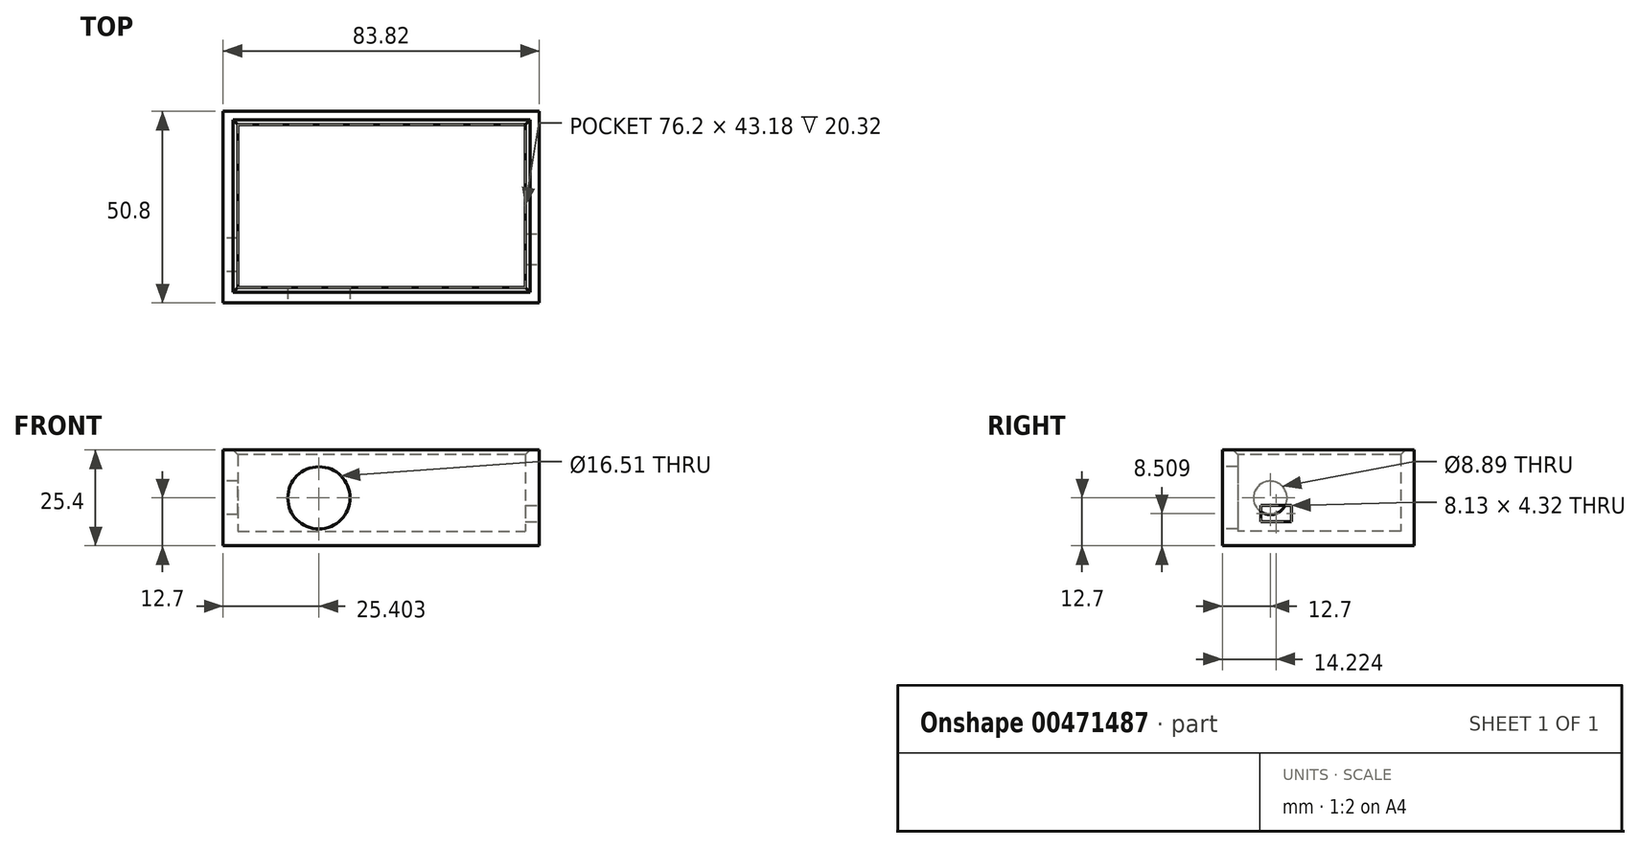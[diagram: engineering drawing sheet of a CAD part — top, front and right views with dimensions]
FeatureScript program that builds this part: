
annotation { "Feature Type Name" : "Feature", "Feature Type Description" : "" }
export const myFeature = defineFeature(function(context is Context, id is Id, definition is map)
    precondition{}
    {
        {
            var Q0;
            Q0=qCreatedBy(makeId("Top.planeOp"),FACE);
            var sketch = newSketch(context, id + "F0", { "sketchPlane" : qUnion([Q0])});
            skLineSegment(sketch, "E0.bottom", {"start": v(-41.04, 23.34) * mm, "end": v(42.78, 23.34) * mm});
            skLineSegment(sketch, "E0.top", {"start": v(-41.04, -27.46) * mm, "end": v(42.78, -27.46) * mm});
            skLineSegment(sketch, "E0.left", {"start": v(-41.04, 23.34) * mm, "end": v(-41.04, -27.46) * mm});
            skLineSegment(sketch, "E0.right", {"start": v(42.78, 23.34) * mm, "end": v(42.78, -27.46) * mm});
            skSolve(sketch);
        }
        {
            var Q0;
            Q0 = qSketchRegion(id + "F0", true);
            extrude(context, id + "F1", {"entities" : qUnion([Q0]), "depth" : 3.8 * mm});
        }
        {
            var Q0;
            Q0=makeQuery(id+"F1.opExtrude","CAP_FACE",FACE,{"disambiguationData":[OSD([sQuery(id+"F0.wireOp",EDGE,"E0.bottom"),sQuery(id+"F0.wireOp",EDGE,"E0.top"),sQuery(id+"F0.wireOp",EDGE,"E0.left"),sQuery(id+"F0.wireOp",EDGE,"E0.right")])],"isStart":false});
            var sketch = newSketch(context, id + "F2", { "sketchPlane" : qUnion([Q0])});
            skLineSegment(sketch, "E1.bottom", {"start": v(-37.08, 19.8) * mm, "end": v(39.12, 19.8) * mm});
            skLineSegment(sketch, "E1.top", {"start": v(-37.08, -23.38) * mm, "end": v(39.12, -23.38) * mm});
            skLineSegment(sketch, "E1.left", {"start": v(-37.08, 19.8) * mm, "end": v(-37.08, -23.38) * mm});
            skLineSegment(sketch, "E1.right", {"start": v(39.12, 19.8) * mm, "end": v(39.12, -23.38) * mm});
            skSolve(sketch);
        }
        {
            var Q0;
            Q0=makeQuery(id+"F2.imprint","IMPRINT",FACE,{"disambiguationData":[TD([[makeQuery(id+"F2.imprint","IMPRINT",EDGE,{"derivedFrom":sQuery(id+"F2.wireOp",EDGE,"E1.bottom")}),1.0]])]});
            extrude(context, id + "F3", {"entities" : qUnion([Q0]), "operationType" : NewBodyOperationType.ADD, "depth" : 21.59 * mm});
        }
        {
            var Q0;
            {var subQ0=sQuery(id+"F0.wireOp",EDGE,"E0.top");Q0=makeQuery(id+"F3.boolean.opBoolean","MERGE",FACE,{"derivedFrom":[makeQuery(id+"F1.opExtrude","SWEPT_FACE",FACE,{"disambiguationData":[OSD([subQ0])]}),makeQuery(id+"F3.opExtrude","SWEPT_FACE",FACE,{"disambiguationData":[OSD([subQ0])]})]});}
            var sketch = newSketch(context, id + "F4", { "sketchPlane" : qUnion([Q0])});
            skCircle(sketch, "E2", {"center": v(-15.64, 12.7) * mm, "radius": 8.26 * mm});
            skLineSegment(sketch, "E3", {"start": v(-41.04, 12.7) * mm, "end": v(-15.64, 12.7) * mm});
            skLineSegment(sketch, "E4", {"start": v(-15.64, 25.4) * mm, "end": v(-15.64, 12.7) * mm});
            skSolve(sketch);
        }
        {
            var Q0;
            Q0 = qSketchRegion(id + "F4", true);
            extrude(context, id + "F5", {"entities" : qUnion([Q0]), "operationType" : NewBodyOperationType.REMOVE, "oppositeDirection" : true, "depth" : 5.08 * mm});
        }
        {
            var Q0;
            {var subQ0=sQuery(id+"F0.wireOp",EDGE,"E0.left");Q0=makeQuery(id+"F3.boolean.opBoolean","MERGE",FACE,{"derivedFrom":[makeQuery(id+"F1.opExtrude","SWEPT_FACE",FACE,{"disambiguationData":[OSD([subQ0])]}),makeQuery(id+"F3.opExtrude","SWEPT_FACE",FACE,{"disambiguationData":[OSD([subQ0])]})]});}
            var sketch = newSketch(context, id + "F6", { "sketchPlane" : qUnion([Q0])});
            skCircle(sketch, "E5", {"center": v(14.76, 12.7) * mm, "radius": 4.45 * mm});
            skLineSegment(sketch, "E6", {"start": v(14.76, 12.7) * mm, "end": v(27.46, 12.7) * mm});
            skPoint(sketch, "E6.endSnap0", {"position": v(27.46, 12.7) * mm});
            skLineSegment(sketch, "E7", {"start": v(14.76, 25.4) * mm, "end": v(14.76, 12.7) * mm});
            skSolve(sketch);
        }
        {
            var Q0;
            Q0 = qSketchRegion(id + "F6", true);
            extrude(context, id + "F7", {"entities" : qUnion([Q0]), "operationType" : NewBodyOperationType.REMOVE, "oppositeDirection" : true, "depth" : 25.4 * mm});
        }
        {
            var Q0;
            Q0=makeQuery(id+"F3.opExtrude","CAP_EDGE",EDGE,{"disambiguationData":[OSD([sQuery(id+"F2.wireOp",EDGE,"E1.bottom")])],"isStart":false});
            var Q1;
            Q1=makeQuery(id+"F3.opExtrude","CAP_EDGE",EDGE,{"disambiguationData":[OSD([sQuery(id+"F2.wireOp",EDGE,"E1.left")])],"isStart":false});
            var Q2;
            Q2=makeQuery(id+"F3.opExtrude","CAP_EDGE",EDGE,{"disambiguationData":[OSD([sQuery(id+"F2.wireOp",EDGE,"E1.top")])],"isStart":false});
            var Q3;
            Q3=makeQuery(id+"F3.opExtrude","CAP_EDGE",EDGE,{"disambiguationData":[OSD([sQuery(id+"F2.wireOp",EDGE,"E1.right")])],"isStart":false});
            chamfer(context, id + "F8", {"entities" : qUnion([Q0, Q1, Q2, Q3]), "chamferType" : ChamferType.TWO_OFFSETS, "width1" : 1.27 * mm, "oppositeDirection" : false, "width2" : 1.27 * mm, "tangentPropagation" : true});
        }
        {
            var Q0;
            {var subQ0=sQuery(id+"F0.wireOp",EDGE,"E0.right");Q0=makeQuery(id+"F3.boolean.opBoolean","MERGE",FACE,{"derivedFrom":[makeQuery(id+"F1.opExtrude","SWEPT_FACE",FACE,{"disambiguationData":[OSD([subQ0])]}),makeQuery(id+"F3.opExtrude","SWEPT_FACE",FACE,{"disambiguationData":[OSD([subQ0])]})]});}
            var sketch = newSketch(context, id + "F9", { "sketchPlane" : qUnion([Q0])});
            skLineSegment(sketch, "E8.bottom", {"start": v(-17.3, 10.67) * mm, "end": v(-9.17, 10.67) * mm});
            skLineSegment(sketch, "E8.top", {"start": v(-17.3, 6.35) * mm, "end": v(-9.17, 6.35) * mm});
            skLineSegment(sketch, "E8.left", {"start": v(-17.3, 10.67) * mm, "end": v(-17.3, 6.35) * mm});
            skLineSegment(sketch, "E8.right", {"start": v(-9.17, 10.67) * mm, "end": v(-9.17, 6.35) * mm});
            skLineSegment(sketch, "E9", {"start": v(-9.17, 6.35) * mm, "end": v(-9.17, 0) * mm});
            skLineSegment(sketch, "E10", {"start": v(-17.3, 6.35) * mm, "end": v(-27.46, 6.35) * mm});
            skSolve(sketch);
        }
        {
            var Q0;
            Q0=makeQuery(id+"F9.imprint","IMPRINT",FACE,{"disambiguationData":[TD([[makeQuery(id+"F9.imprint","IMPRINT",EDGE,{"derivedFrom":sQuery(id+"F9.wireOp",EDGE,"E8.bottom")}),-1.0]])]});
            extrude(context, id + "F10", {"entities" : qUnion([Q0]), "operationType" : NewBodyOperationType.REMOVE, "oppositeDirection" : true, "depth" : 25.4 * mm});
        }
    });
